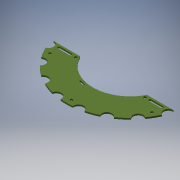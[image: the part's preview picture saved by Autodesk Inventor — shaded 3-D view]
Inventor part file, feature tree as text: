
AUTODESK INVENTOR PART (.ipt)
format: ipt  version: 2016 (Build 200138000, 138)  size: 186,368 bytes
history: native  units: mm
features: extrude x4, sketch x3, mirror x1, reference x1
ambient origin geometry x8: Origin, YZ Plane, XZ Plane, XY Plane, X Axis, Y Axis, Z Axis, Center Point
bodies: Solid1 (feature_tree)
feature tree (9):
  extrude  "Extrusion1"  TaperAngle=0.0deg  [1 undecoded]
  extrude  "Extrusion2"  TaperAngle=0.0deg  [1 undecoded]
  extrude  "Extrusion3"  Depth=1.75mm
  mirror  "Mirror1"
  extrude  "Extrusion4"  TaperAngle=0.0deg  [1 undecoded]
  reference  "Reference1"
  sketch  "Sketch2"  dims[d0=1.75mm d1=0.0mm]
  sketch  "Sketch3"  dims[d2=1.75mm d3=0.0mm]
  sketch  "Sketch4"  dims[d4=3.0mm d5=1.75mm d6=0.0mm d7=2.0mm d8=5.0mm d9=2.0mm d10=1.75mm d11=0.0mm]
note: 3 required parameter values undecoded (feature->parameter linkage not recoverable at this tier; creation-order binding heuristic only, values carry confidence <= 0.55)
